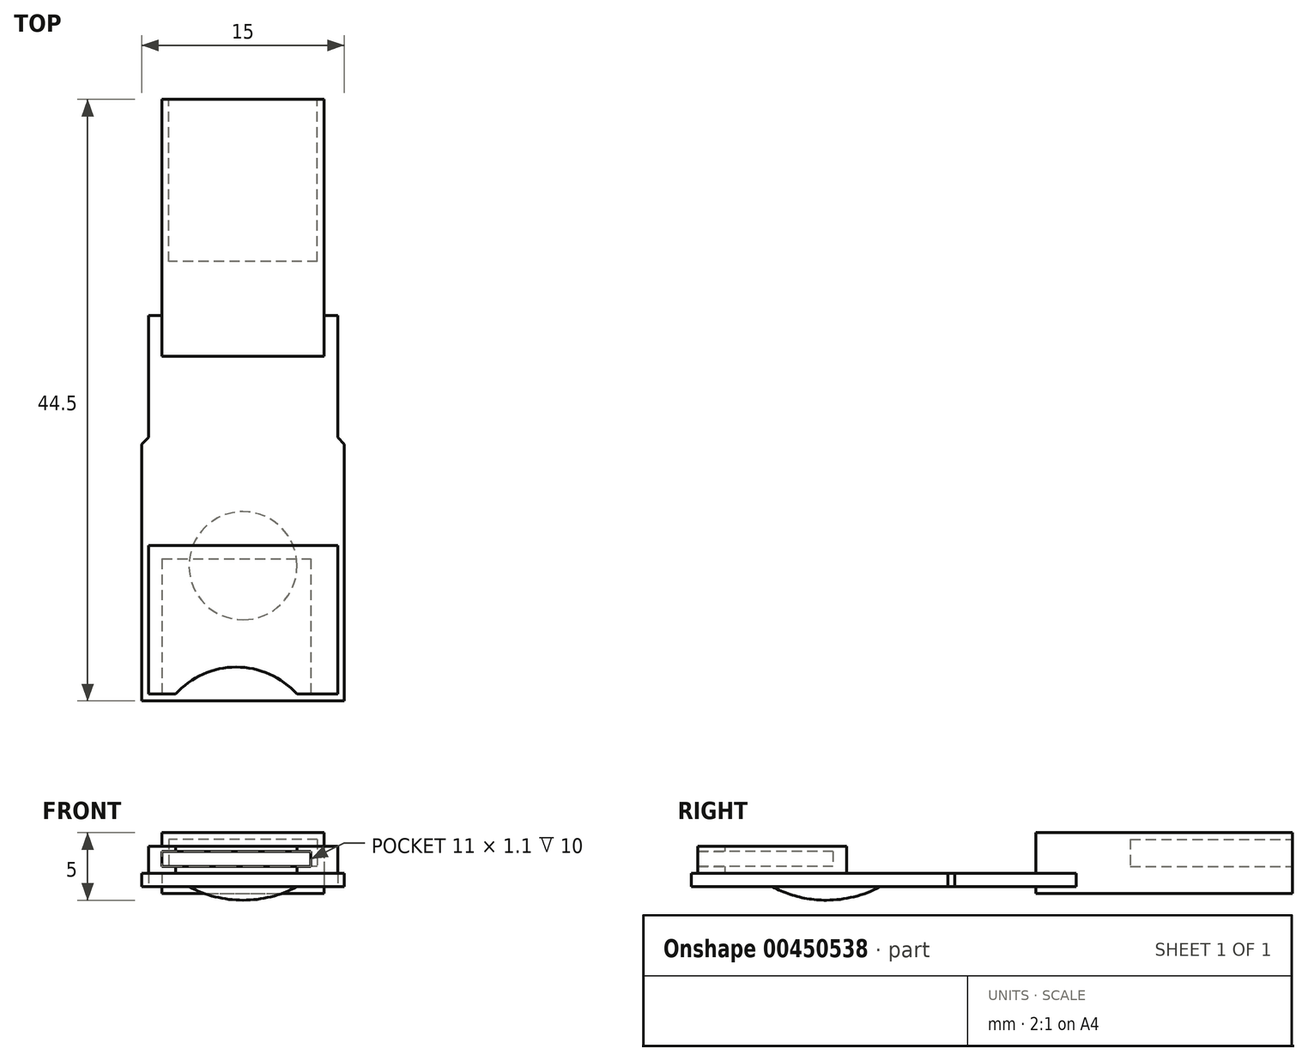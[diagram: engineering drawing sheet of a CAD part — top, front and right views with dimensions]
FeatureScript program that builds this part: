
annotation { "Feature Type Name" : "Feature", "Feature Type Description" : "" }
export const myFeature = defineFeature(function(context is Context, id is Id, definition is map)
    precondition{}
    {
        {
            var Q0;
            Q0=qCreatedBy(makeId("Top.planeOp"),FACE);
            var sketch = newSketch(context, id + "F0", { "sketchPlane" : qUnion([Q0])});
            skLineSegment(sketch, "E0.top", {"start": v(-7.5, -19) * mm, "end": v(7.5, -19) * mm});
            skLineSegment(sketch, "E0.left", {"start": v(-7.5, 0) * mm, "end": v(-7.5, -19) * mm});
            skLineSegment(sketch, "E0.right", {"start": v(7.5, 0) * mm, "end": v(7.5, -19) * mm});
            skLineSegment(sketch, "E1", {"start": v(-7.5, 0) * mm, "end": v(-7, 0.5) * mm});
            skLineSegment(sketch, "E2", {"start": v(-7, 0.5) * mm, "end": v(-7, 9.5) * mm});
            skLineSegment(sketch, "E3", {"start": v(-7, 9.5) * mm, "end": v(-6, 9.5) * mm});
            skLineSegment(sketch, "E4", {"start": v(-6, 9.5) * mm, "end": v(-6, 25.5) * mm});
            skLineSegment(sketch, "E5", {"start": v(-6, 25.5) * mm, "end": v(6, 25.5) * mm});
            skLineSegment(sketch, "E6", {"start": v(6, 25.5) * mm, "end": v(6, 9.5) * mm});
            skLineSegment(sketch, "E7", {"start": v(6, 9.5) * mm, "end": v(7, 9.5) * mm});
            skLineSegment(sketch, "E8", {"start": v(7, 9.5) * mm, "end": v(7, 0.5) * mm});
            skLineSegment(sketch, "E9", {"start": v(7, 0.5) * mm, "end": v(7.5, 0) * mm});
            skSolve(sketch);
        }
        {
            var Q0;
            Q0 = qSketchRegion(id + "F0", true);
            extrude(context, id + "F1", {"entities" : qUnion([Q0]), "depth" : 1 * mm});
        }
        {
            var Q0;
            Q0=makeQuery(id+"F1.opExtrude","CAP_FACE",FACE,{"disambiguationData":[OSD([sQuery(id+"F0.wireOp",EDGE,"E0.top"),sQuery(id+"F0.wireOp",EDGE,"E0.left"),sQuery(id+"F0.wireOp",EDGE,"E0.right"),sQuery(id+"F0.wireOp",EDGE,"E1"),sQuery(id+"F0.wireOp",EDGE,"E2"),sQuery(id+"F0.wireOp",EDGE,"E3"),sQuery(id+"F0.wireOp",EDGE,"E4"),sQuery(id+"F0.wireOp",EDGE,"E5"),sQuery(id+"F0.wireOp",EDGE,"E6"),sQuery(id+"F0.wireOp",EDGE,"E7"),sQuery(id+"F0.wireOp",EDGE,"E8"),sQuery(id+"F0.wireOp",EDGE,"E9")])],"isStart":true});
            var sketch = newSketch(context, id + "F2", { "sketchPlane" : qUnion([Q0])});
            skLineSegment(sketch, "E10.bottom", {"start": v(-6, -25.5) * mm, "end": v(6, -25.5) * mm});
            skLineSegment(sketch, "E10.top", {"start": v(-6, -6.5) * mm, "end": v(6, -6.5) * mm});
            skLineSegment(sketch, "E10.left", {"start": v(-6, -25.5) * mm, "end": v(-6, -6.5) * mm});
            skLineSegment(sketch, "E10.right", {"start": v(6, -25.5) * mm, "end": v(6, -6.5) * mm});
            skSolve(sketch);
        }
        {
            var Q0;
            {var subQ3=sQuery(id+"F2.wireOp",EDGE,"E10.bottom");Q0=makeQuery(id+"F2.imprint","IMPRINT",FACE,{"disambiguationData":[TD([[makeQuery(id+"F2.imprint","IMPRINT",EDGE,{"derivedFrom":subQ3}),1.0]])]});}
            extrude(context, id + "F3", {"entities" : qUnion([Q0]), "operationType" : NewBodyOperationType.ADD, "oppositeDirection" : true, "depth" : 4 * mm});
        }
        {
            var Q0;
            Q0 = qSketchRegion(id + "F2", true);
            extrude(context, id + "F4", {"entities" : qUnion([Q0]), "operationType" : NewBodyOperationType.ADD, "depth" : .5 * mm});
        }
        {
            var Q0;
            Q0=qCreatedBy(makeId("Right.planeOp"),FACE);
            var sketch = newSketch(context, id + "F5", { "sketchPlane" : qUnion([Q0])});
            skLineSegment(sketch, "E11", {"start": v(-13, 0) * mm, "end": v(-9, 0) * mm});
            skLineSegment(sketch, "E12", {"start": v(-9, 0) * mm, "end": v(-9, -1) * mm});
            skLineSegment(sketch, "E13", {"start": v(-9, -1) * mm, "end": v(-0.17, -1) * mm, "construction": true});
            skArc(sketch, "E14", {"start": v(-9, -1) * mm, "mid": v(-11.06, -0.75) * mm, "end": v(-13, 0) * mm});
            skSolve(sketch);
        }
        {
            var Q0;
            Q0 = qSketchRegion(id + "F5", true);
            var Q1;
            Q1=sQuery(id+"F5.wireOp",EDGE,"E12");
            revolve(context, id + "F6", {"operationType" : NewBodyOperationType.ADD, "entities" : qUnion([Q0]), "axis" : qUnion([Q1]), "revolveType" : RevolveType.FULL});
        }
        {
            var Q0;
            Q0=makeQuery(id+"F1.opExtrude","CAP_FACE",FACE,{"disambiguationData":[OSD([sQuery(id+"F0.wireOp",EDGE,"E0.top"),sQuery(id+"F0.wireOp",EDGE,"E0.left"),sQuery(id+"F0.wireOp",EDGE,"E0.right"),sQuery(id+"F0.wireOp",EDGE,"E1"),sQuery(id+"F0.wireOp",EDGE,"E2"),sQuery(id+"F0.wireOp",EDGE,"E3"),sQuery(id+"F0.wireOp",EDGE,"E4"),sQuery(id+"F0.wireOp",EDGE,"E5"),sQuery(id+"F0.wireOp",EDGE,"E6"),sQuery(id+"F0.wireOp",EDGE,"E7"),sQuery(id+"F0.wireOp",EDGE,"E8"),sQuery(id+"F0.wireOp",EDGE,"E9")])],"isStart":false});
            var sketch = newSketch(context, id + "F7", { "sketchPlane" : qUnion([Q0])});
            skLineSegment(sketch, "E15.bottom", {"start": v(7, -18.5) * mm, "end": v(4, -18.5) * mm});
            skLineSegment(sketch, "E15.top", {"start": v(7, -7.5) * mm, "end": v(-7, -7.5) * mm});
            skLineSegment(sketch, "E15.left", {"start": v(7, -18.5) * mm, "end": v(7, -7.5) * mm});
            skLineSegment(sketch, "E15.right", {"start": v(-7, -18.5) * mm, "end": v(-7, -7.5) * mm});
            skArc(sketch, "E16", {"start": v(4, -18.5) * mm, "mid": v(-0.5, -16.5) * mm, "end": v(-5, -18.5) * mm});
            skLineSegment(sketch, "E17", {"start": v(7, -16.5) * mm, "end": v(-7, -16.5) * mm, "construction": true});
            skLineSegment(sketch, "E18.trimOffspring", {"start": v(-5, -18.5) * mm, "end": v(-7, -18.5) * mm});
            skSolve(sketch);
        }
        {
            var Q0;
            Q0 = qSketchRegion(id + "F7", true);
            extrude(context, id + "F8", {"entities" : qUnion([Q0]), "operationType" : NewBodyOperationType.ADD, "offsetDistance" : 25.4 * mm, "depth" : 2 * mm});
        }
        {
            var Q0;
            Q0=makeQuery(id+"F8.opExtrude","SWEPT_FACE",FACE,{"disambiguationData":[OSD([sQuery(id+"F7.wireOp",EDGE,"E18.trimOffspring")])]});
            var sketch = newSketch(context, id + "F9", { "sketchPlane" : qUnion([Q0])});
            skLineSegment(sketch, "E19.bottom", {"start": v(-6, 2.6) * mm, "end": v(5, 2.6) * mm});
            skLineSegment(sketch, "E19.top", {"start": v(-6, 1.5) * mm, "end": v(5, 1.5) * mm});
            skLineSegment(sketch, "E19.left", {"start": v(-6, 2.6) * mm, "end": v(-6, 1.5) * mm});
            skLineSegment(sketch, "E19.right", {"start": v(5, 2.6) * mm, "end": v(5, 1.5) * mm});
            skSolve(sketch);
        }
        {
            var Q0;
            Q0 = qSketchRegion(id + "F9", true);
            var Q1;
            Q1=makeQuery(id+"F8.opExtrude","SWEPT_FACE",FACE,{"disambiguationData":[OSD([sQuery(id+"F7.wireOp",EDGE,"E15.top")])]});
            extrude(context, id + "F10", {"entities" : qUnion([Q0]), "operationType" : NewBodyOperationType.REMOVE, "oppositeDirection" : true, "endBoundEntityFace" : qUnion([Q1]), "depth" : 10 * mm});
        }
        {
            var Q0;
            {var subQ0=sQuery(id+"F2.wireOp",EDGE,"E10.bottom");Q0=makeQuery(id+"F4.boolean.opBoolean","MERGE",FACE,{"derivedFrom":[makeQuery(id+"F3.boolean.opBoolean","MERGE",FACE,{"derivedFrom":[makeQuery(id+"F1.opExtrude","SWEPT_FACE",FACE,{"disambiguationData":[OSD([sQuery(id+"F0.wireOp",EDGE,"E5")])]}),makeQuery(id+"F3.opExtrude","SWEPT_FACE",FACE,{"disambiguationData":[OSD([subQ0])]})]}),makeQuery(id+"F4.opExtrude","SWEPT_FACE",FACE,{"disambiguationData":[OSD([subQ0])]})]});}
            var sketch = newSketch(context, id + "F11", { "sketchPlane" : qUnion([Q0])});
            skLineSegment(sketch, "E20.bottom", {"start": v(-5.5, 3.5) * mm, "end": v(5.5, 3.5) * mm});
            skLineSegment(sketch, "E20.top", {"start": v(-5.5, 1.5) * mm, "end": v(5.5, 1.5) * mm});
            skLineSegment(sketch, "E20.left", {"start": v(-5.5, 3.5) * mm, "end": v(-5.5, 1.5) * mm});
            skLineSegment(sketch, "E20.right", {"start": v(5.5, 3.5) * mm, "end": v(5.5, 1.5) * mm});
            skSolve(sketch);
        }
        {
            var Q0;
            Q0 = qSketchRegion(id + "F11", true);
            extrude(context, id + "F12", {"entities" : qUnion([Q0]), "operationType" : NewBodyOperationType.REMOVE, "oppositeDirection" : true, "offsetDistance" : 25.4 * mm, "depth" : 12 * mm});
        }
    });
